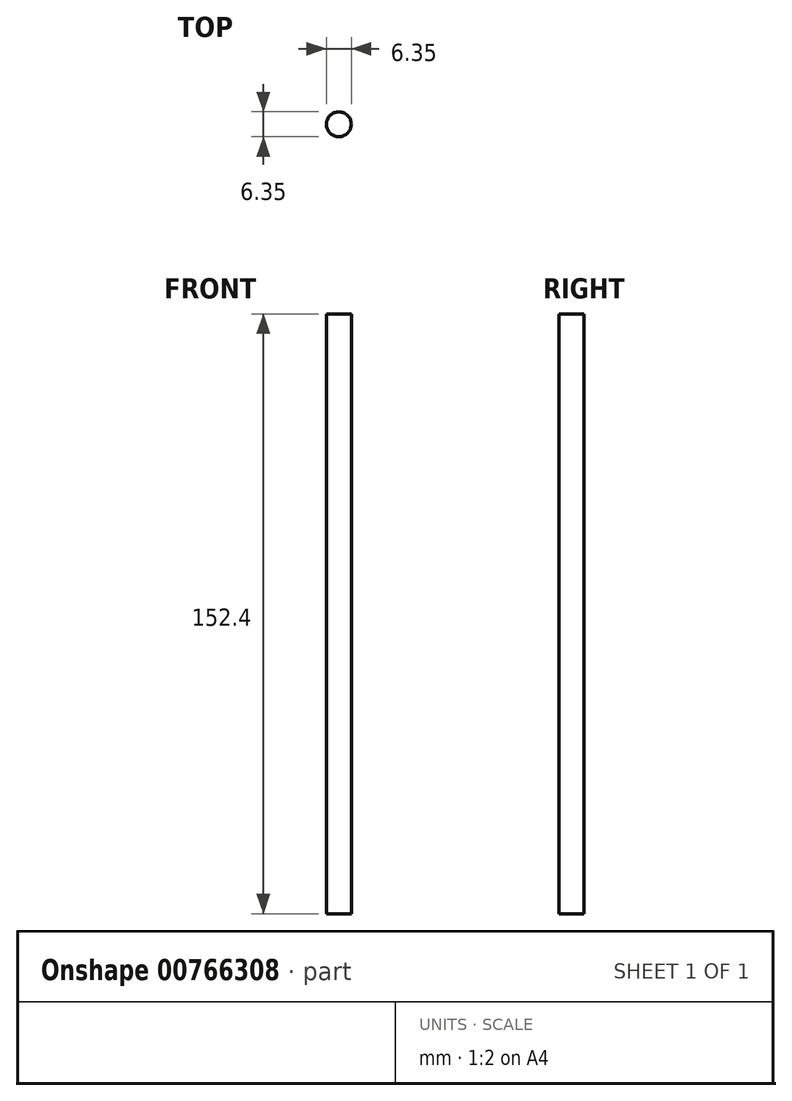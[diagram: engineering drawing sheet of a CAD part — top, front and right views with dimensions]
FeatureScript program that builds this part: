
annotation { "Feature Type Name" : "Feature", "Feature Type Description" : "" }
export const myFeature = defineFeature(function(context is Context, id is Id, definition is map)
    precondition{}
    {
        {
            var Q0;
            Q0=qCreatedBy(makeId("Top.planeOp"),FACE);
            var sketch = newSketch(context, id + "F0", { "sketchPlane" : qUnion([Q0])});
            skCircle(sketch, "E0", {"center": v(23.03, 15.56) * mm, "radius": 3.18 * mm});
            skSolve(sketch);
        }
        {
            var Q0;
            Q0=makeQuery(id+"F0.imprint","IMPRINT",FACE,{"disambiguationData":[TD([[makeQuery(id+"F0.imprint","IMPRINT",EDGE,{"derivedFrom":sQuery(id+"F0.wireOp",EDGE,"E0")}),1.0]])]});
            var Q1;
            Q1=sQuery(id+"F0.wireOp",EDGE,"E0");
            extrude(context, id + "F1", {"entities" : qUnion([Q0]), "surfaceEntities" : qUnion([Q1]), "depth" : 152.4 * mm, "offsetDistance" : 25.4 * mm});
        }
    });
